SOLIDWORKS PART (.sldprt)
format: sldprt  version: not decoded by parser v0  size: 96,768 bytes
history: native  units: mm
features: sketch x5, plane x4, extrude x2, cut_extrude x2, material x1, fillet x1 (+13 scaffold rows collapsed)
feature tree (28):
  scaffold x13  (default folders/planes/origin — collapsed)
  material  "材质 <未指定>"
  plane  "前视基准面"
  plane  "上视基准面"
  plane  "右视基准面"
  sketch  "草图1"  dims[D1=~0.47955mm]
  extrude  "凸台-拉伸1"  Depth=0.8mm
  sketch  "草图2"
  plane  "基准面1"
  sketch  "草图3"  dims[D2=0.6mm D1=0.4mm]
  extrude  "凸台-拉伸4"  Depth=4.5mm
  sketch  "草图7"  dims[D1=0.3mm]
  cut_extrude  "切除-拉伸3"  Depth=4.5mm
  fillet  "圆角1"  Radius=0.3mm
  sketch  "草图8"
  cut_extrude  "凸台-拉伸5"  Depth=0.8mm
decode coverage: 8 of 10 modeling features carry decoded parameters
note: ~ marks probable driven/reference dimensions
note: suppression state not decoded; provenance and decode notes live in map.json
